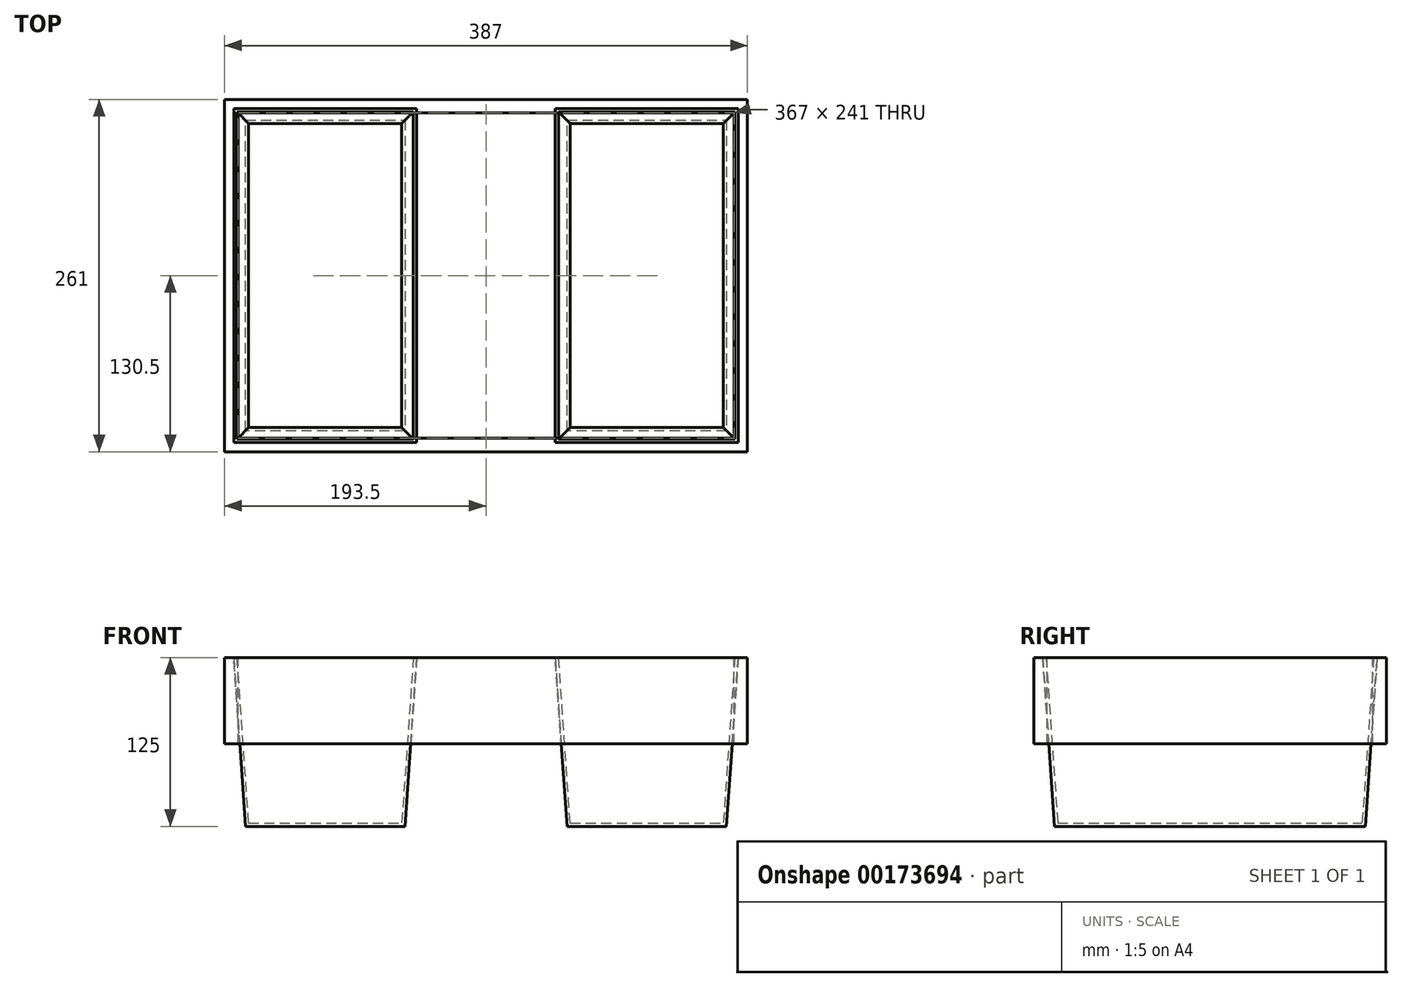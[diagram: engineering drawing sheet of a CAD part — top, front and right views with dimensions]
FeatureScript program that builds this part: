
annotation { "Feature Type Name" : "Feature", "Feature Type Description" : "" }
export const myFeature = defineFeature(function(context is Context, id is Id, definition is map)
    precondition{}
    {
        {
            var Q0;
            Q0=qCreatedBy(makeId("Top.planeOp"),FACE);
            var sketch = newSketch(context, id + "F0", { "sketchPlane" : qUnion([Q0])});
            skLineSegment(sketch, "E0.bottom", {"start": v(59, -115) * mm, "end": v(-59, -115) * mm, "construction": true});
            skLineSegment(sketch, "E0.top", {"start": v(59, 115) * mm, "end": v(-59, 115) * mm, "construction": true});
            skLineSegment(sketch, "E0.left", {"start": v(59, -115) * mm, "end": v(59, 115) * mm, "construction": true});
            skLineSegment(sketch, "E0.right", {"start": v(-59, -115) * mm, "end": v(-59, 115) * mm, "construction": true});
            skPoint(sketch, "E0.middle", {"position": v(0, 0) * mm});
            skLineSegment(sketch, "E1.bottom", {"start": v(60, 115) * mm, "end": v(178, 115) * mm});
            skLineSegment(sketch, "E1.top", {"start": v(60, -115) * mm, "end": v(178, -115) * mm});
            skLineSegment(sketch, "E1.left", {"start": v(60, 115) * mm, "end": v(60, -115) * mm});
            skLineSegment(sketch, "E1.right", {"start": v(178, 115) * mm, "end": v(178, -115) * mm});
            skPoint(sketch, "E1.middle", {"position": v(119, 0) * mm});
            skLineSegment(sketch, "E2.bottom", {"start": v(-178, 115) * mm, "end": v(-60, 115) * mm});
            skLineSegment(sketch, "E2.top", {"start": v(-178, -115) * mm, "end": v(-60, -115) * mm});
            skLineSegment(sketch, "E2.left", {"start": v(-178, 115) * mm, "end": v(-178, -115) * mm});
            skLineSegment(sketch, "E2.right", {"start": v(-60, 115) * mm, "end": v(-60, -115) * mm});
            skPoint(sketch, "E2.middle", {"position": v(-119, 0) * mm});
            skSolve(sketch);
        }
        {
            var Q0;
            Q0=qSketchRegion(id+"F0",true);
            extrude(context, id + "F1", {"entities" : qUnion([Q0]), "depth" : 125 * mm, "hasDraft" : true, "draftAngle" : 4 * degree});
        }
        {
            var Q0;
            Q0=makeQuery(id+"F1.opExtrude","CAP_FACE",FACE,{"disambiguationData":[OSD([sQuery(id+"F0.wireOp",EDGE,"E2.bottom"),sQuery(id+"F0.wireOp",EDGE,"E2.top"),sQuery(id+"F0.wireOp",EDGE,"E2.left"),sQuery(id+"F0.wireOp",EDGE,"E2.right")])],"isStart":false});
            var sketch = newSketch(context, id + "F2", { "sketchPlane" : qUnion([Q0])});
            skLineSegment(sketch, "E3.bottom", {"start": v(183.5, -120.5) * mm, "end": v(-183.5, -120.5) * mm});
            skLineSegment(sketch, "E3.top", {"start": v(183.5, 120.5) * mm, "end": v(-183.5, 120.5) * mm});
            skLineSegment(sketch, "E3.left", {"start": v(183.5, -120.5) * mm, "end": v(183.5, 120.5) * mm});
            skLineSegment(sketch, "E3.right", {"start": v(-183.5, -120.5) * mm, "end": v(-183.5, 120.5) * mm});
            skPoint(sketch, "E3.middle", {"position": v(0, 0) * mm});
            skLineSegment(sketch, "E4.bottom", {"start": v(193.5, -130.5) * mm, "end": v(-193.5, -130.5) * mm});
            skLineSegment(sketch, "E4.top", {"start": v(193.5, 130.5) * mm, "end": v(-193.5, 130.5) * mm});
            skLineSegment(sketch, "E4.left", {"start": v(193.5, -130.5) * mm, "end": v(193.5, 130.5) * mm});
            skLineSegment(sketch, "E4.right", {"start": v(-193.5, -130.5) * mm, "end": v(-193.5, 130.5) * mm});
            skSolve(sketch);
        }
        {
            var Q0;
            Q0=qSketchRegion(id+"F2",true);
            extrude(context, id + "F3", {"entities" : qUnion([Q0]), "oppositeDirection" : true, "depth" : 64 * mm});
        }
        {
            var Q0;
            Q0=makeQuery(id+"F1.opExtrude","CAP_FACE",FACE,{"disambiguationData":[OSD([sQuery(id+"F0.wireOp",EDGE,"E2.bottom"),sQuery(id+"F0.wireOp",EDGE,"E2.top"),sQuery(id+"F0.wireOp",EDGE,"E2.left"),sQuery(id+"F0.wireOp",EDGE,"E2.right")])],"isStart":false});
            var Q1;
            Q1=makeQuery(id+"F1.opExtrude","CAP_FACE",FACE,{"disambiguationData":[OSD([sQuery(id+"F0.wireOp",EDGE,"E1.bottom"),sQuery(id+"F0.wireOp",EDGE,"E1.top"),sQuery(id+"F0.wireOp",EDGE,"E1.left"),sQuery(id+"F0.wireOp",EDGE,"E1.right")])],"isStart":false});
            shell(context, id + "F4", {"entities" : qUnion([Q0, Q1]), "thickness" : 2.5 * mm});
        }
    });
